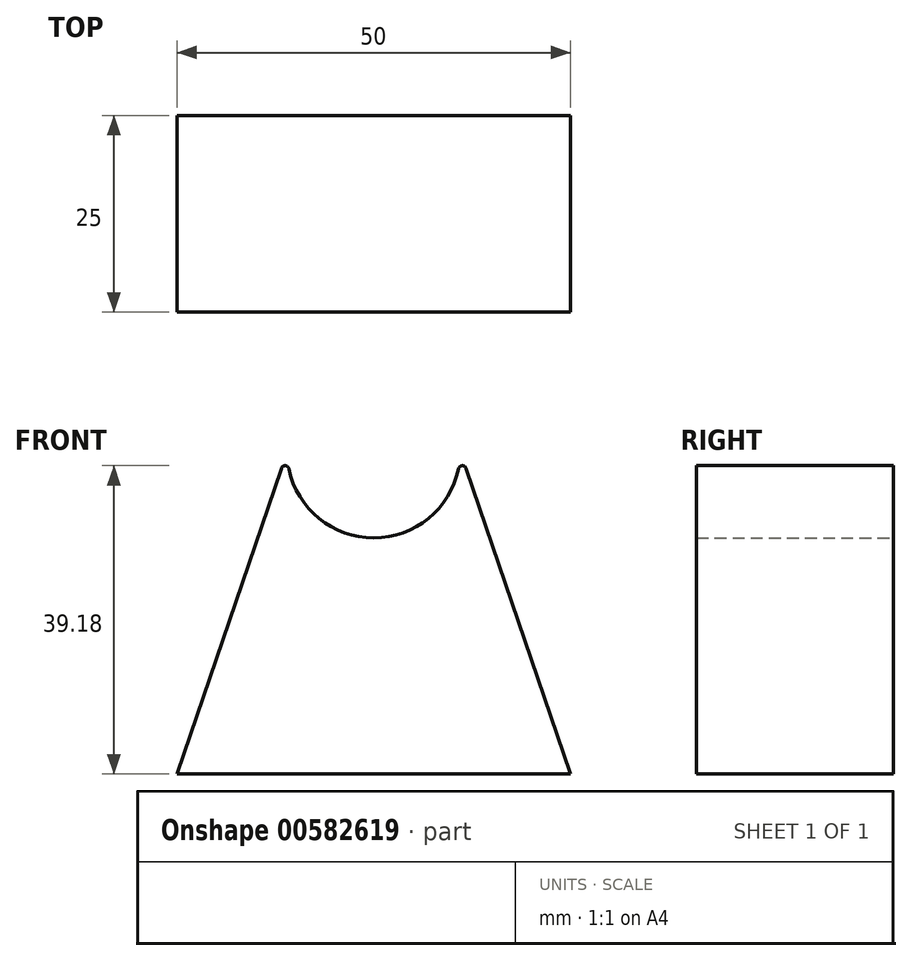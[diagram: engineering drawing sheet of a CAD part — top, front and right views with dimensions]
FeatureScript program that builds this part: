
annotation { "Feature Type Name" : "Feature", "Feature Type Description" : "" }
export const myFeature = defineFeature(function(context is Context, id is Id, definition is map)
    precondition{}
    {
        {
            var Q0;
            Q0=qCreatedBy(makeId("Front.planeOp"),FACE);
            var sketch = newSketch(context, id + "F0", { "sketchPlane" : qUnion([Q0])});
            skCircle(sketch, "E0", {"center": v(0, 41) * mm, "radius": 11 * mm});
            skLineSegment(sketch, "E1", {"start": v(-25, 0) * mm, "end": v(25, 0) * mm});
            skLineSegment(sketch, "E2", {"start": v(25, 0) * mm, "end": v(0, 73.21) * mm});
            skLineSegment(sketch, "E3", {"start": v(0, 73.21) * mm, "end": v(-25, 0) * mm});
            skLineSegment(sketch, "E4", {"start": v(0, 41) * mm, "end": v(11, 41) * mm, "construction": true});
            skLineSegment(sketch, "E5", {"start": v(0, 41) * mm, "end": v(-11, 41) * mm, "construction": true});
            skSolve(sketch);
        }
        {
            var Q0;
            {var subQ5=sQuery(id+"F0.wireOp",EDGE,"E1");Q0=makeQuery(id+"F0.imprint","IMPRINT",FACE,{"disambiguationData":[TD([[makeQuery(id+"F0.imprint","IMPRINT",EDGE,{"derivedFrom":subQ5}),1.0]])]});}
            extrude(context, id + "F1", {"entities" : qUnion([Q0]), "depth" : 25 * mm, "offsetDistance" : 25 * mm});
        }
        {
            var Q0;
            Q0=makeQuery(id+"F1.opExtrude","SWEPT_EDGE",EDGE,{"disambiguationData":[OSD([sQuery(id+"F0.wireOp",EDGE,"E0"),sQuery(id+"F0.wireOp",EDGE,"E3")])]});
            var Q1;
            Q1=makeQuery(id+"F1.opExtrude","SWEPT_EDGE",EDGE,{"disambiguationData":[OSD([sQuery(id+"F0.wireOp",EDGE,"E0"),sQuery(id+"F0.wireOp",EDGE,"E2")])]});
            fillet(context, id + "F2", {"entities" : qUnion([Q0, Q1]), "radius" : 0.5 * mm, "tangentPropagation" : true, "allowEdgeOverflow" : false});
        }
    });
